# Revit family: ledflood-e2_re253-50w-4000-bl_543017011700
name_source: partatom
category: Leuchten
revit_build: Autodesk Revit 2016 (Build: 20190508_0715(x64)
units: mm (PartAtom-declared; Revit-internal decimal feet)

## family parameters
Basisbauteil = Fläche
Beim Laden mit Abzugskörper schneiden = Nein
Bemaßung runder Anschluss = Durchmesser verwenden
Gemeinsam genutzt = Nein
Lichtquelle = Nein
Raumberechnungspunkt = Nein
Teiletyp = Normal

## types (1)
- LEDFlood-E2 Re253-50W-4000-BL (1 x LED, 6000 lm)
    Approval mark = CE
    Beschreibung = Slim aluminium body with integrated heatsink and clipless cover. Robust and water- and dustproof. High energy saving compared to halogen and high pressure sodium lamps. Compatible brackets, ground spikes and other installation accessories available. IP65 daylight and motion sensor accessory available.
    CIE Flux Codes = 53 84 98 100 100
    Control Gear = Electronic ballast
    Height = 46 mm
    Hersteller = OPPLE
    Lamp Light Flux = 6000 lm
    Lamp count = 1
    Lampe = 1 x LED
    Length = 205 mm
    Luminous efficacy = 120 lm/W
    ModVariant = Nein
    Modell = 543017011700
    Mounting Place = Wall
    Mounting Type = Surface mounted
    Number of Poles = 1
    OnlyDefault = Ja
    Power Factor = 1
    Product Name = LEDFlood-E2 Re253-50W-4000-BL
    Product group = Floodlight EcoMax G2 Medium Power
    ProductGroupID = 2004
    Protection Class = Protection class I
    Protection Degree = IP 66
    RLX_Detail_Level = 1
    RlxData = <blob elided: 163565 chars, md5=8f0cad55>
    Scheinlast = 50 VA
    Socket = socket
    Standby Power = 0 W
    System Light Flux = 6000 lm
    System Power = 50 W
    Typenbild = 543017011700.jpg
    Typenkommentare = Product without accessories
    URL = http://relux.com
    VarID = ---
    Voltage = 0 V
    Vorgabe-Ansicht = 1800 mm
    Weight = 0.00 kg
    Width = 228 mm

## geometry (parser evidence)
native form markers: Blend x4, Sweep x11
no freeform markers — native parametric forms only
